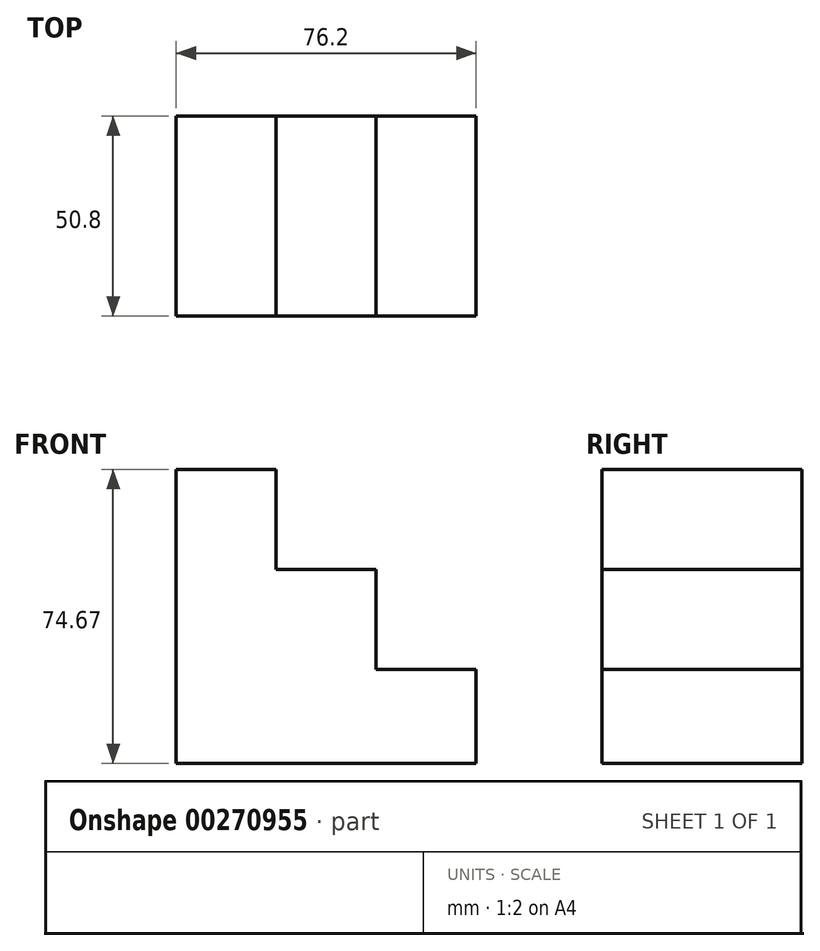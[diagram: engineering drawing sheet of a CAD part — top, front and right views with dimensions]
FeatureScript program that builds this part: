
annotation { "Feature Type Name" : "Feature", "Feature Type Description" : "" }
export const myFeature = defineFeature(function(context is Context, id is Id, definition is map)
    precondition{}
    {
        {
            var Q0;
            Q0=qCreatedBy(makeId("Front.planeOp"),FACE);
            var sketch = newSketch(context, id + "F0", { "sketchPlane" : qUnion([Q0])});
            skLineSegment(sketch, "E0", {"start": v(-69.5, 50.8) * mm, "end": v(-69.5, 0) * mm});
            skLineSegment(sketch, "E1", {"start": v(-69.5, 50.8) * mm, "end": v(-44.1, 50.8) * mm});
            skLineSegment(sketch, "E2", {"start": v(-44.1, 50.8) * mm, "end": v(-44.1, 25.4) * mm});
            skLineSegment(sketch, "E3", {"start": v(-44.1, 25.4) * mm, "end": v(-18.7, 25.4) * mm});
            skLineSegment(sketch, "E4", {"start": v(-18.7, 25.4) * mm, "end": v(-18.7, 0) * mm});
            skLineSegment(sketch, "E5", {"start": v(-18.7, 0) * mm, "end": v(6.7, 0) * mm});
            skLineSegment(sketch, "E6", {"start": v(6.7, 1.53) * mm, "end": v(6.7, -23.87) * mm});
            skLineSegment(sketch, "E7", {"start": v(-69.5, 0) * mm, "end": v(-69.5, -23.87) * mm});
            skLineSegment(sketch, "E8", {"start": v(-69.5, -23.87) * mm, "end": v(6.7, -23.87) * mm});
            skSolve(sketch);
        }
        {
            var Q0;
            Q0 = qSketchRegion(id + "F0", true);
            extrude(context, id + "F1", {"entities" : qUnion([Q0]), "depth" : 50.8 * mm});
        }
    });
